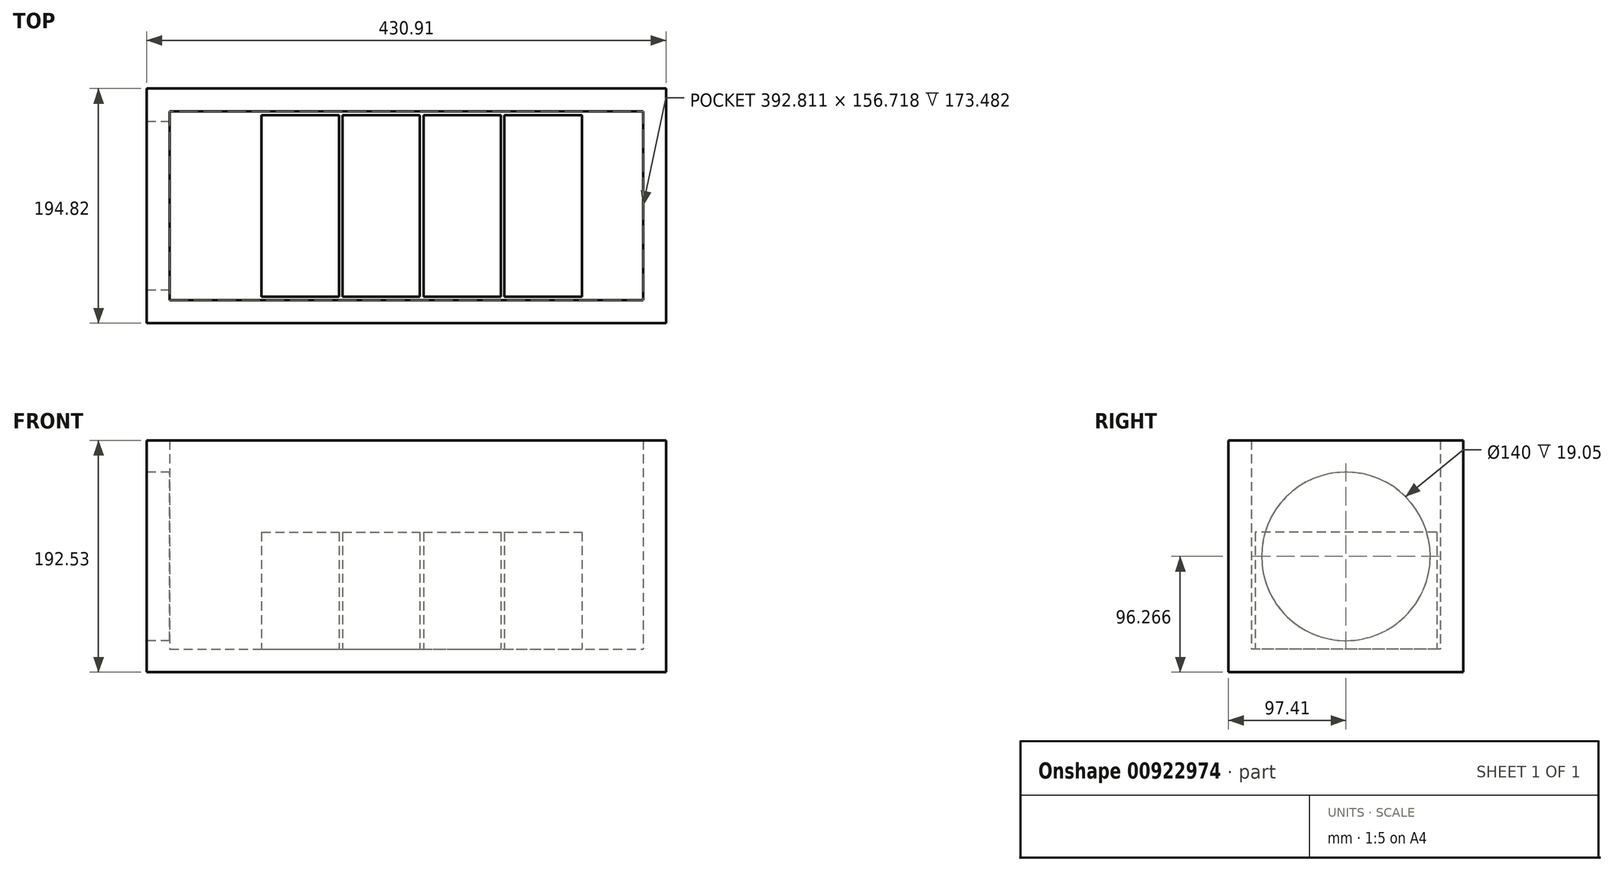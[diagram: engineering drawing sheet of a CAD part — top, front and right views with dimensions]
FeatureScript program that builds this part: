
annotation { "Feature Type Name" : "Feature", "Feature Type Description" : "" }
export const myFeature = defineFeature(function(context is Context, id is Id, definition is map)
    precondition{}
    {
        {
            var Q0;
            Q0=qCreatedBy(makeId("Top.planeOp"),FACE);
            var sketch = newSketch(context, id + "F0", { "sketchPlane" : qUnion([Q0])});
            skLineSegment(sketch, "E0.bottom", {"start": v(-32.13, 75.44) * mm, "end": v(32.13, 75.44) * mm});
            skLineSegment(sketch, "E0.top", {"start": v(-32.13, -75.44) * mm, "end": v(32.13, -75.44) * mm});
            skLineSegment(sketch, "E0.left", {"start": v(-32.13, 75.44) * mm, "end": v(-32.13, -75.44) * mm});
            skLineSegment(sketch, "E0.right", {"start": v(32.13, 75.44) * mm, "end": v(32.13, -75.44) * mm});
            skPoint(sketch, "E0.middle", {"position": v(0, 0) * mm});
            skSolve(sketch);
        }
        {
            var Q0;
            Q0=makeQuery(id+"F0.imprint","IMPRINT",FACE,{"disambiguationData":[TD([[makeQuery(id+"F0.imprint","IMPRINT",EDGE,{"derivedFrom":sQuery(id+"F0.wireOp",EDGE,"E0.bottom")}),-1.0]])]});
            extrude(context, id + "F1", {"entities" : qUnion([Q0]), "depth" : 97.28 * mm, "offsetDistance" : 25.4 * mm});
        }
        {
            var Q0;
            Q0=qCreatedBy(makeId("Top.planeOp"),FACE);
            var sketch = newSketch(context, id + "F2", { "sketchPlane" : qUnion([Q0])});
            skLineSegment(sketch, "E1.bottom", {"start": v(-99.31, 75.44) * mm, "end": v(-35.05, 75.44) * mm});
            skLineSegment(sketch, "E1.top", {"start": v(-99.31, -75.44) * mm, "end": v(-35.05, -75.44) * mm});
            skLineSegment(sketch, "E1.left", {"start": v(-99.31, 75.44) * mm, "end": v(-99.31, -75.44) * mm});
            skLineSegment(sketch, "E1.right", {"start": v(-35.05, 75.44) * mm, "end": v(-35.05, -75.44) * mm});
            skPoint(sketch, "E1.middle", {"position": v(-84.07, 0.13) * mm});
            skSolve(sketch);
        }
        {
            var Q0;
            Q0=makeQuery(id+"F2.imprint","IMPRINT",FACE,{"disambiguationData":[TD([[makeQuery(id+"F2.imprint","IMPRINT",EDGE,{"derivedFrom":sQuery(id+"F2.wireOp",EDGE,"E1.bottom")}),-1.0]])]});
            extrude(context, id + "F3", {"entities" : qUnion([Q0]), "depth" : 97.28 * mm, "offsetDistance" : 25.4 * mm});
        }
        {
            var Q0;
            Q0=qCreatedBy(makeId("Top.planeOp"),FACE);
            var sketch = newSketch(context, id + "F4", { "sketchPlane" : qUnion([Q0])});
            skLineSegment(sketch, "E2.bottom", {"start": v(35.05, 75.44) * mm, "end": v(99.31, 75.44) * mm});
            skLineSegment(sketch, "E2.top", {"start": v(35.05, -75.44) * mm, "end": v(99.31, -75.44) * mm});
            skLineSegment(sketch, "E2.left", {"start": v(35.05, 75.44) * mm, "end": v(35.05, -75.44) * mm});
            skLineSegment(sketch, "E2.right", {"start": v(99.31, 75.44) * mm, "end": v(99.31, -75.44) * mm});
            skPoint(sketch, "E2.middle", {"position": v(82.42, 0.22) * mm});
            skSolve(sketch);
        }
        {
            var Q0;
            Q0=makeQuery(id+"F4.imprint","IMPRINT",FACE,{"disambiguationData":[TD([[makeQuery(id+"F4.imprint","IMPRINT",EDGE,{"derivedFrom":sQuery(id+"F4.wireOp",EDGE,"E2.bottom")}),-1.0]])]});
            extrude(context, id + "F5", {"entities" : qUnion([Q0]), "depth" : 97.28 * mm, "offsetDistance" : 25.4 * mm});
        }
        {
            var Q0;
            Q0=qCreatedBy(makeId("Top.planeOp"),FACE);
            var sketch = newSketch(context, id + "F6", { "sketchPlane" : qUnion([Q0])});
            skLineSegment(sketch, "E3.bottom", {"start": v(102.24, 75.44) * mm, "end": v(166.5, 75.44) * mm});
            skLineSegment(sketch, "E3.top", {"start": v(102.24, -75.44) * mm, "end": v(166.5, -75.44) * mm});
            skLineSegment(sketch, "E3.left", {"start": v(102.24, 75.44) * mm, "end": v(102.24, -75.44) * mm});
            skLineSegment(sketch, "E3.right", {"start": v(166.5, 75.44) * mm, "end": v(166.5, -75.44) * mm});
            skPoint(sketch, "E3.middle", {"position": v(150.88, 0.78) * mm});
            skSolve(sketch);
        }
        {
            var Q0;
            Q0=makeQuery(id+"F6.imprint","IMPRINT",FACE,{"disambiguationData":[TD([[makeQuery(id+"F6.imprint","IMPRINT",EDGE,{"derivedFrom":sQuery(id+"F6.wireOp",EDGE,"E3.bottom")}),-1.0]])]});
            extrude(context, id + "F7", {"entities" : qUnion([Q0]), "depth" : 97.28 * mm, "offsetDistance" : 25.4 * mm});
        }
        {
            var Q0;
            Q0=qCreatedBy(makeId("Top.planeOp"),FACE);
            var sketch = newSketch(context, id + "F8", { "sketchPlane" : qUnion([Q0])});
            skLineSegment(sketch, "E4.bottom", {"start": v(-175.51, 78.36) * mm, "end": v(217.3, 78.36) * mm});
            skLineSegment(sketch, "E4.top", {"start": v(-175.51, -78.36) * mm, "end": v(217.3, -78.36) * mm});
            skLineSegment(sketch, "E4.left", {"start": v(-175.51, 78.36) * mm, "end": v(-175.51, -78.36) * mm});
            skLineSegment(sketch, "E4.right", {"start": v(217.3, 78.36) * mm, "end": v(217.3, -78.36) * mm});
            skSolve(sketch);
        }
        {
            var Q0;
            Q0=makeQuery(id+"F8.imprint","IMPRINT",FACE,{"disambiguationData":[TD([[makeQuery(id+"F8.imprint","IMPRINT",EDGE,{"derivedFrom":sQuery(id+"F8.wireOp",EDGE,"E4.bottom")}),-1.0]])]});
            extrude(context, id + "F9", {"entities" : qUnion([Q0]), "depth" : 173.48 * mm, "offsetDistance" : 25.4 * mm});
        }
        {
            var Q0;
            Q0=makeQuery(id+"F9.opExtrude","CAP_FACE",FACE,{"disambiguationData":[OSD([sQuery(id+"F8.wireOp",EDGE,"E4.bottom"),sQuery(id+"F8.wireOp",EDGE,"E4.top"),sQuery(id+"F8.wireOp",EDGE,"E4.left"),sQuery(id+"F8.wireOp",EDGE,"E4.right")])],"isStart":false});
            shell(context, id + "F10", {"entities" : qUnion([Q0]), "thickness" : 19.05 * mm, "oppositeDirection" : true});
        }
        {
            var Q0;
            Q0=makeQuery(id+"F9.opExtrude","SWEPT_FACE",FACE,{"disambiguationData":[OSD([sQuery(id+"F8.wireOp",EDGE,"E4.left")])]});
            var sketch = newSketch(context, id + "F11", { "sketchPlane" : qUnion([Q0])});
            skPoint(sketch, "E5", {"position": v(0, 77.22) * mm});
            skPoint(sketch, "E5.positionSnap0", {"position": v(97.4, 77.22) * mm});
            skSolve(sketch);
        }
        {
            var Q0;
            Q0=sQuery(id+"F11.wireOp",VERTEX,"E5");
            var Q1;
            Q1=makeQuery(id+"F9.opExtrude","SWEPT_BODY",BODY,{"disambiguationData":[OSD([sQuery(id+"F8.wireOp",EDGE,"E4.bottom"),sQuery(id+"F8.wireOp",EDGE,"E4.top"),sQuery(id+"F8.wireOp",EDGE,"E4.left"),sQuery(id+"F8.wireOp",EDGE,"E4.right")])]});
            hole(context, id + "F12", {"style" : HoleStyle.SIMPLE, "endStyle" : HoleEndStyle.BLIND, "holeDiameter" : 140 * mm, "majorDiameter" : 6.35 * mm, "holeDepth" : 25.4 * mm, "isTappedThrough" : true, "tappedDepth" : 12.7 * mm, "tapClearance" : 3, "locations" : qUnion([Q0]), "scope" : qUnion([Q1])});
        }
    });
